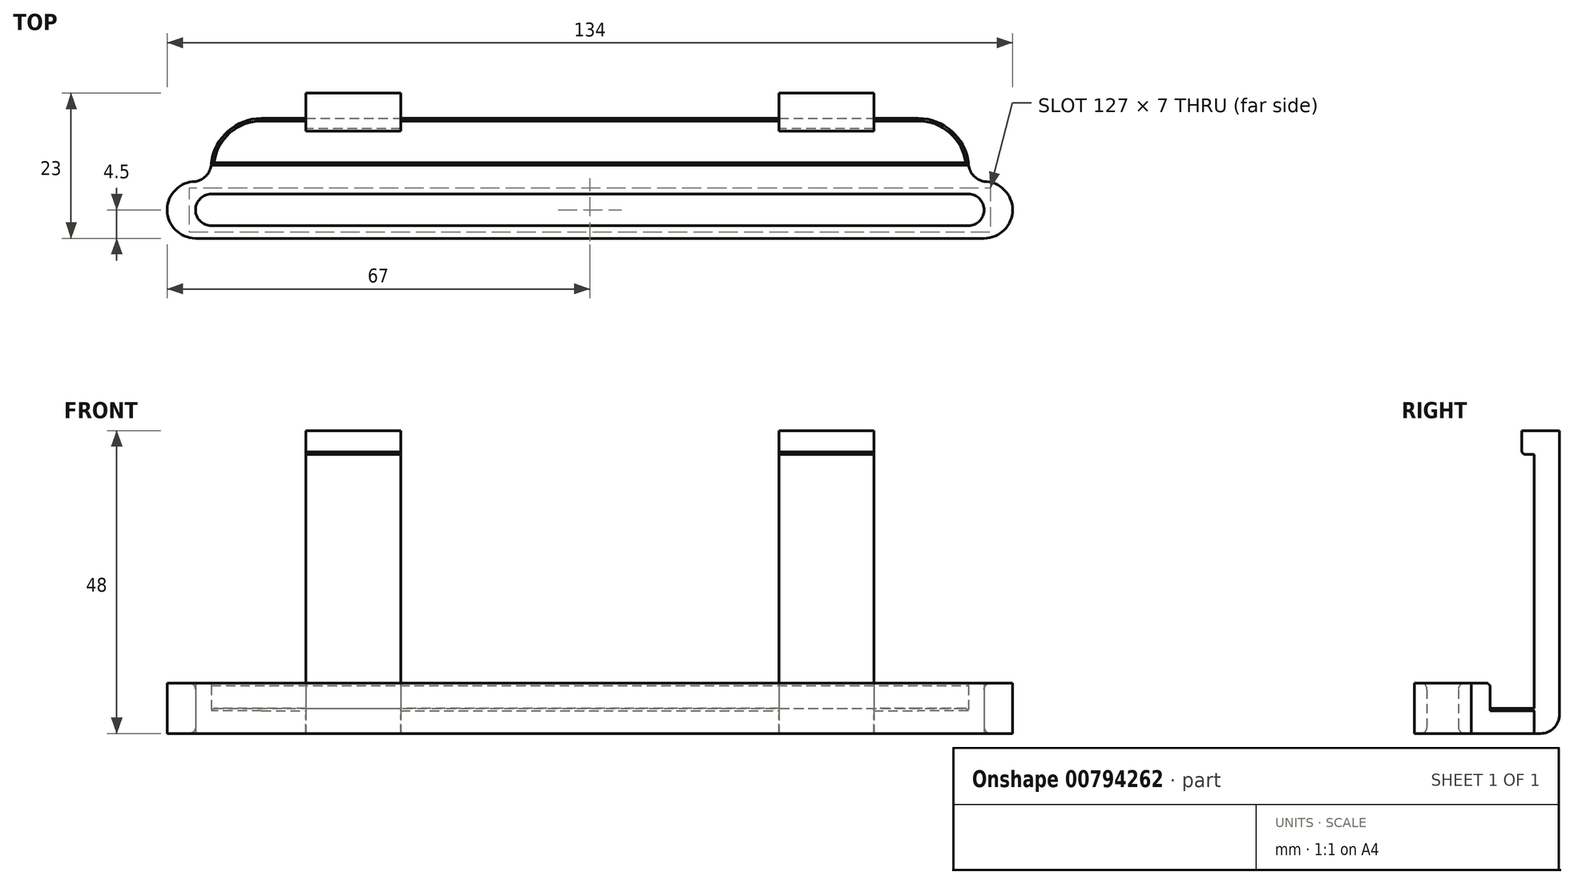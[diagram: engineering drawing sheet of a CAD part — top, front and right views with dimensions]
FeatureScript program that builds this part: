
annotation { "Feature Type Name" : "Feature", "Feature Type Description" : "" }
export const myFeature = defineFeature(function(context is Context, id is Id, definition is map)
    precondition{}
    {
        {
            var Q0;
            Q0=qCreatedBy(makeId("Top.planeOp"),FACE);
            var sketch = newSketch(context, id + "F0", { "sketchPlane" : qUnion([Q0])});
            skLineSegment(sketch, "E0.bottom", {"start": v(-60, 0) * mm, "end": v(60, 0) * mm});
            skLineSegment(sketch, "E0.top", {"start": v(-60, -5) * mm, "end": v(60, -5) * mm});
            skLineSegment(sketch, "E0.left", {"start": v(-60, 0) * mm, "end": v(-60, -5) * mm});
            skLineSegment(sketch, "E0.right", {"start": v(60, 0) * mm, "end": v(60, -5) * mm});
            skArc(sketch, "E1", {"start": v(60, -5) * mm, "mid": v(62.5, -2.5) * mm, "end": v(60, 0) * mm});
            skArc(sketch, "E2", {"start": v(-60, 0) * mm, "mid": v(-62.5, -2.5) * mm, "end": v(-60, -5) * mm});
            skPoint(sketch, "E3.firstSnap0", {"position": v(-62.5, -2.5) * mm});
            skLineSegment(sketch, "E3.bottom", {"start": v(-62.5, 2) * mm, "end": v(62.5, 2) * mm});
            skLineSegment(sketch, "E3.top", {"start": v(-62.5, -7) * mm, "end": v(62.5, -7) * mm});
            skLineSegment(sketch, "E3.left", {"start": v(-62.5, 2) * mm, "end": v(-62.5, -7) * mm});
            skLineSegment(sketch, "E3.right", {"start": v(62.5, 2) * mm, "end": v(62.5, -7) * mm});
            skArc(sketch, "E4", {"start": v(-62.5, 2) * mm, "mid": v(-67, -2.5) * mm, "end": v(-62.5, -7) * mm});
            skArc(sketch, "E5", {"start": v(62.5, -7) * mm, "mid": v(67, -2.5) * mm, "end": v(62.5, 2) * mm});
            skLineSegment(sketch, "E6.bottom", {"start": v(-60, 12) * mm, "end": v(60, 12) * mm});
            skLineSegment(sketch, "E6.top", {"start": v(-60, 5) * mm, "end": v(60, 5) * mm});
            skLineSegment(sketch, "E6.left", {"start": v(-60, 12) * mm, "end": v(-60, 5) * mm});
            skLineSegment(sketch, "E6.right", {"start": v(60, 12) * mm, "end": v(60, 5) * mm});
            skArc(sketch, "E7", {"start": v(-62.5, 2) * mm, "mid": v(-60.7, 3.05) * mm, "end": v(-60, 5) * mm});
            skArc(sketch, "E8", {"start": v(60, 5) * mm, "mid": v(60.7, 3.05) * mm, "end": v(62.5, 2) * mm});
            skLineSegment(sketch, "E9.bottom", {"start": v(-45, 16) * mm, "end": v(-30, 16) * mm});
            skLineSegment(sketch, "E9.top", {"start": v(-45, 12) * mm, "end": v(-30, 12) * mm});
            skLineSegment(sketch, "E9.left", {"start": v(-45, 16) * mm, "end": v(-45, 12) * mm});
            skLineSegment(sketch, "E9.right", {"start": v(-30, 16) * mm, "end": v(-30, 12) * mm});
            skPoint(sketch, "E10", {"position": v(-30, 12) * mm});
            skLineSegment(sketch, "E11.MirrorCS", {"start": v(45, 16) * mm, "end": v(30, 16) * mm});
            skLineSegment(sketch, "E12.MirrorCS", {"start": v(45, 12) * mm, "end": v(30, 12) * mm});
            skPoint(sketch, "E13.MirrorP", {"position": v(30, 12) * mm});
            skLineSegment(sketch, "E14.MirrorCS", {"start": v(30, 16) * mm, "end": v(30, 12) * mm});
            skLineSegment(sketch, "E15.MirrorCS", {"start": v(45, 16) * mm, "end": v(45, 12) * mm});
            skSolve(sketch);
        }
        {
            var Q0;
            {var subQ2=sQuery(id+"F0.wireOp",EDGE,"E0.top");Q0=makeQuery(id+"F0.imprint","IMPRINT",FACE,{"disambiguationData":[TD([[makeQuery(id+"F0.imprint","IMPRINT",EDGE,{"derivedFrom":subQ2}),-1.0]])]});}
            var Q1;
            {var subQ2=sQuery(id+"F0.wireOp",EDGE,"E5");Q1=makeQuery(id+"F0.imprint","IMPRINT",FACE,{"disambiguationData":[TD([[makeQuery(id+"F0.imprint","IMPRINT",EDGE,{"derivedFrom":subQ2}),1.0]])]});}
            var Q2;
            {var subQ0=sQuery(id+"F0.wireOp",EDGE,"E4");Q2=makeQuery(id+"F0.imprint","IMPRINT",FACE,{"disambiguationData":[TD([[makeQuery(id+"F0.imprint","IMPRINT",EDGE,{"derivedFrom":subQ0}),1.0]])]});}
            var Q3;
            {var subQ2=sQuery(id+"F0.wireOp",EDGE,"E0.bottom");Q3=makeQuery(id+"F0.imprint","IMPRINT",FACE,{"disambiguationData":[TD([[makeQuery(id+"F0.imprint","IMPRINT",EDGE,{"derivedFrom":subQ2}),1.0]])]});}
            extrude(context, id + "F1", {"entities" : qUnion([Q0, Q1, Q2, Q3]), "depth" : 8 * mm, "offsetDistance" : 25 * mm});
        }
        {
            var Q0;
            Q0=makeQuery(id+"F0.imprint","IMPRINT",FACE,{"disambiguationData":[TD([[makeQuery(id+"F0.imprint","IMPRINT",EDGE,{"derivedFrom":sQuery(id+"F0.wireOp",EDGE,"E3.bottom")}),1.0]])]});
            extrude(context, id + "F2", {"entities" : qUnion([Q0]), "operationType" : NewBodyOperationType.ADD, "depth" : 8 * mm, "offsetDistance" : 25 * mm});
        }
        {
            var Q0;
            Q0=makeQuery(id+"F0.imprint","IMPRINT",FACE,{"disambiguationData":[TD([[makeQuery(id+"F0.imprint","IMPRINT",EDGE,{"derivedFrom":sQuery(id+"F0.wireOp",EDGE,"E6.top")}),1.0]])]});
            extrude(context, id + "F3", {"entities" : qUnion([Q0]), "operationType" : NewBodyOperationType.ADD, "depth" : 4 * mm, "offsetDistance" : 25 * mm});
        }
        {
            var Q0;
            Q0=makeQuery(id+"F0.imprint","IMPRINT",FACE,{"disambiguationData":[TD([[makeQuery(id+"F0.imprint","IMPRINT",EDGE,{"derivedFrom":sQuery(id+"F0.wireOp",EDGE,"E9.bottom")}),-1.0]])]});
            var Q1;
            Q1=makeQuery(id+"F0.imprint","IMPRINT",FACE,{"disambiguationData":[TD([[makeQuery(id+"F0.imprint","IMPRINT",EDGE,{"derivedFrom":sQuery(id+"F0.wireOp",EDGE,"E11.MirrorCS")}),1.0]])]});
            extrude(context, id + "F4", {"entities" : qUnion([Q0, Q1]), "operationType" : NewBodyOperationType.ADD, "depth" : 48 * mm, "offsetDistance" : 25 * mm});
        }
        {
            var Q0;
            {var subQ0=sQuery(id+"F0.wireOp",EDGE,"E6.bottom");Q0=makeQuery(id+"F4.opExtrude","SWEPT_FACE",FACE,{"disambiguationData":[OSD([subQ0]),TDD([makeQuery(id+"F0.imprint","IMPRINT",EDGE,{"disambiguationData":[TD([[makeQuery(id+"F0.imprint","INTERSECT",VERTEX,{"derivedFrom":[subQ0,sQuery(id+"F0.wireOp",EDGE,"E9.right")]}),1.0]])],"derivedFrom":subQ0})])]});}
            var sketch = newSketch(context, id + "F5", { "sketchPlane" : qUnion([Q0])});
            skLineSegment(sketch, "E16.bottom", {"start": v(-45, 48) * mm, "end": v(-30, 48) * mm});
            skLineSegment(sketch, "E16.top", {"start": v(-45, 44.25) * mm, "end": v(-30, 44.25) * mm});
            skLineSegment(sketch, "E16.left", {"start": v(-45, 48) * mm, "end": v(-45, 44.25) * mm});
            skLineSegment(sketch, "E16.right", {"start": v(-30, 48) * mm, "end": v(-30, 44.25) * mm});
            skLineSegment(sketch, "E17.MirrorCS", {"start": v(30, 48) * mm, "end": v(30, 44.25) * mm});
            skLineSegment(sketch, "E18.MirrorCS", {"start": v(45, 48) * mm, "end": v(45, 44.25) * mm});
            skLineSegment(sketch, "E19.MirrorCS", {"start": v(45, 48) * mm, "end": v(30, 48) * mm});
            skLineSegment(sketch, "E20.MirrorCS", {"start": v(45, 44.25) * mm, "end": v(30, 44.25) * mm});
            skSolve(sketch);
        }
        {
            var Q0;
            Q0=makeQuery(id+"F5.imprint","IMPRINT",FACE,{"disambiguationData":[TD([[makeQuery(id+"F5.imprint","IMPRINT",EDGE,{"derivedFrom":sQuery(id+"F5.wireOp",EDGE,"E16.bottom")}),-1.0]])]});
            var Q1;
            Q1=makeQuery(id+"F5.imprint","IMPRINT",FACE,{"disambiguationData":[TD([[makeQuery(id+"F5.imprint","IMPRINT",EDGE,{"derivedFrom":sQuery(id+"F5.wireOp",EDGE,"E17.MirrorCS")}),1.0]])]});
            extrude(context, id + "F6", {"entities" : qUnion([Q0, Q1]), "operationType" : NewBodyOperationType.ADD, "depth" : 2 * mm, "offsetDistance" : 25 * mm});
        }
        {
            var Q0;
            Q0=makeQuery(id+"F3.opExtrude","SWEPT_EDGE",EDGE,{"disambiguationData":[OSD([sQuery(id+"F0.wireOp",EDGE,"E6.bottom"),sQuery(id+"F0.wireOp",EDGE,"E6.right")])]});
            var Q1;
            Q1=makeQuery(id+"F3.opExtrude","SWEPT_EDGE",EDGE,{"disambiguationData":[OSD([sQuery(id+"F0.wireOp",EDGE,"E6.bottom"),sQuery(id+"F0.wireOp",EDGE,"E6.left")])]});
            fillet(context, id + "F7", {"entities" : qUnion([Q0, Q1]), "tangentPropagation" : true, "radius" : 8 * mm, "defaultsChanged" : true, "vertexSettings" : [], "allowEdgeOverflow" : false});
        }
        {
            var Q0;
            Q0=makeQuery(id+"F1.opExtrude","CAP_EDGE",EDGE,{"disambiguationData":[OSD([sQuery(id+"F0.wireOp",EDGE,"E0.bottom")])],"isStart":false});
            fillet(context, id + "F8", {"entities" : qUnion([Q0]), "tangentPropagation" : true, "radius" : 1 * mm, "defaultsChanged" : true, "vertexSettings" : [], "allowEdgeOverflow" : false});
        }
        {
            var Q0;
            Q0=makeQuery(id+"F1.opExtrude","CAP_EDGE",EDGE,{"disambiguationData":[OSD([sQuery(id+"F0.wireOp",EDGE,"E0.top")])],"isStart":true});
            fillet(context, id + "F9", {"entities" : qUnion([Q0]), "tangentPropagation" : true, "radius" : 1 * mm, "defaultsChanged" : true, "vertexSettings" : [], "allowEdgeOverflow" : false});
        }
        {
            var Q0;
            Q0=makeQuery(id+"F4.opExtrude","CAP_EDGE",EDGE,{"disambiguationData":[OSD([sQuery(id+"F0.wireOp",EDGE,"E9.bottom")])],"isStart":true});
            var Q1;
            Q1=makeQuery(id+"F4.opExtrude","CAP_EDGE",EDGE,{"disambiguationData":[OSD([sQuery(id+"F0.wireOp",EDGE,"E11.MirrorCS")])],"isStart":true});
            fillet(context, id + "F10", {"entities" : qUnion([Q0, Q1]), "tangentPropagation" : true, "radius" : 3 * mm, "defaultsChanged" : true, "vertexSettings" : [], "allowEdgeOverflow" : false});
        }
        {
            var Q0;
            Q0=makeQuery(id+"F3.opExtrude","CAP_EDGE",EDGE,{"disambiguationData":[OSD([sQuery(id+"F0.wireOp",EDGE,"E6.top")])],"isStart":false});
            var Q1;
            {var subQ0=sQuery(id+"F0.wireOp",EDGE,"E6.bottom");Q1=makeQuery(id+"F4.boolean.opBoolean","SPLIT",EDGE,{"disambiguationData":[topologyDisambiguationEdgeConnected([makeQuery(id+"F3.opExtrude","CAP_FACE",FACE,{"disambiguationData":[OSD([subQ0,sQuery(id+"F0.wireOp",EDGE,"E6.top"),sQuery(id+"F0.wireOp",EDGE,"E6.left"),sQuery(id+"F0.wireOp",EDGE,"E6.right")])],"isStart":false}),makeQuery(id+"F4.opExtrude","SWEPT_FACE",FACE,{"disambiguationData":[OSD([subQ0]),TDD([makeQuery(id+"F0.imprint","IMPRINT",EDGE,{"disambiguationData":[TD([[makeQuery(id+"F0.imprint","INTERSECT",VERTEX,{"derivedFrom":[subQ0,sQuery(id+"F0.wireOp",EDGE,"E9.right")]}),1.0]])],"derivedFrom":subQ0})])]})])],"derivedFrom":makeQuery(id+"F3.opExtrude","CAP_EDGE",EDGE,{"disambiguationData":[OSD([subQ0])],"isStart":false})});}
            var Q2;
            {var subQ0=sQuery(id+"F0.wireOp",EDGE,"E6.bottom");Q2=makeQuery(id+"F4.boolean.opBoolean","SPLIT",EDGE,{"disambiguationData":[topologyDisambiguationEdgeConnected([makeQuery(id+"F3.opExtrude","CAP_FACE",FACE,{"disambiguationData":[OSD([subQ0,sQuery(id+"F0.wireOp",EDGE,"E6.top"),sQuery(id+"F0.wireOp",EDGE,"E6.left"),sQuery(id+"F0.wireOp",EDGE,"E6.right")])],"isStart":false}),makeQuery(id+"F4.opExtrude","SWEPT_FACE",FACE,{"disambiguationData":[OSD([subQ0]),TDD([makeQuery(id+"F0.imprint","IMPRINT",EDGE,{"disambiguationData":[TD([[makeQuery(id+"F0.imprint","INTERSECT",VERTEX,{"derivedFrom":[subQ0,sQuery(id+"F0.wireOp",EDGE,"E14.MirrorCS")]}),-1.0]])],"derivedFrom":subQ0})])]})])],"derivedFrom":makeQuery(id+"F3.opExtrude","CAP_EDGE",EDGE,{"disambiguationData":[OSD([subQ0])],"isStart":false})});}
            var Q3;
            Q3=makeQuery(id+"F2.opExtrude","CAP_EDGE",EDGE,{"disambiguationData":[OSD([sQuery(id+"F0.wireOp",EDGE,"E6.top")])],"isStart":false});
            var Q4;
            Q4=makeQuery(id+"F6.opExtrude","CAP_EDGE",EDGE,{"disambiguationData":[OSD([sQuery(id+"F5.wireOp",EDGE,"E20.MirrorCS")])],"isStart":true});
            var Q5;
            Q5=makeQuery(id+"F6.opExtrude","CAP_EDGE",EDGE,{"disambiguationData":[OSD([sQuery(id+"F5.wireOp",EDGE,"E16.top")])],"isStart":true});
            var Q6;
            Q6=makeQuery(id+"F6.opExtrude","CAP_EDGE",EDGE,{"disambiguationData":[OSD([sQuery(id+"F5.wireOp",EDGE,"E16.top")])],"isStart":false});
            var Q7;
            Q7=makeQuery(id+"F6.opExtrude","CAP_EDGE",EDGE,{"disambiguationData":[OSD([sQuery(id+"F5.wireOp",EDGE,"E20.MirrorCS")])],"isStart":false});
            chamfer(context, id + "F11", {"entities" : qUnion([Q0, Q1, Q2, Q3, Q4, Q5, Q6, Q7]), "width" : 0.4 * mm, "tangentPropagation" : true});
        }
    });
